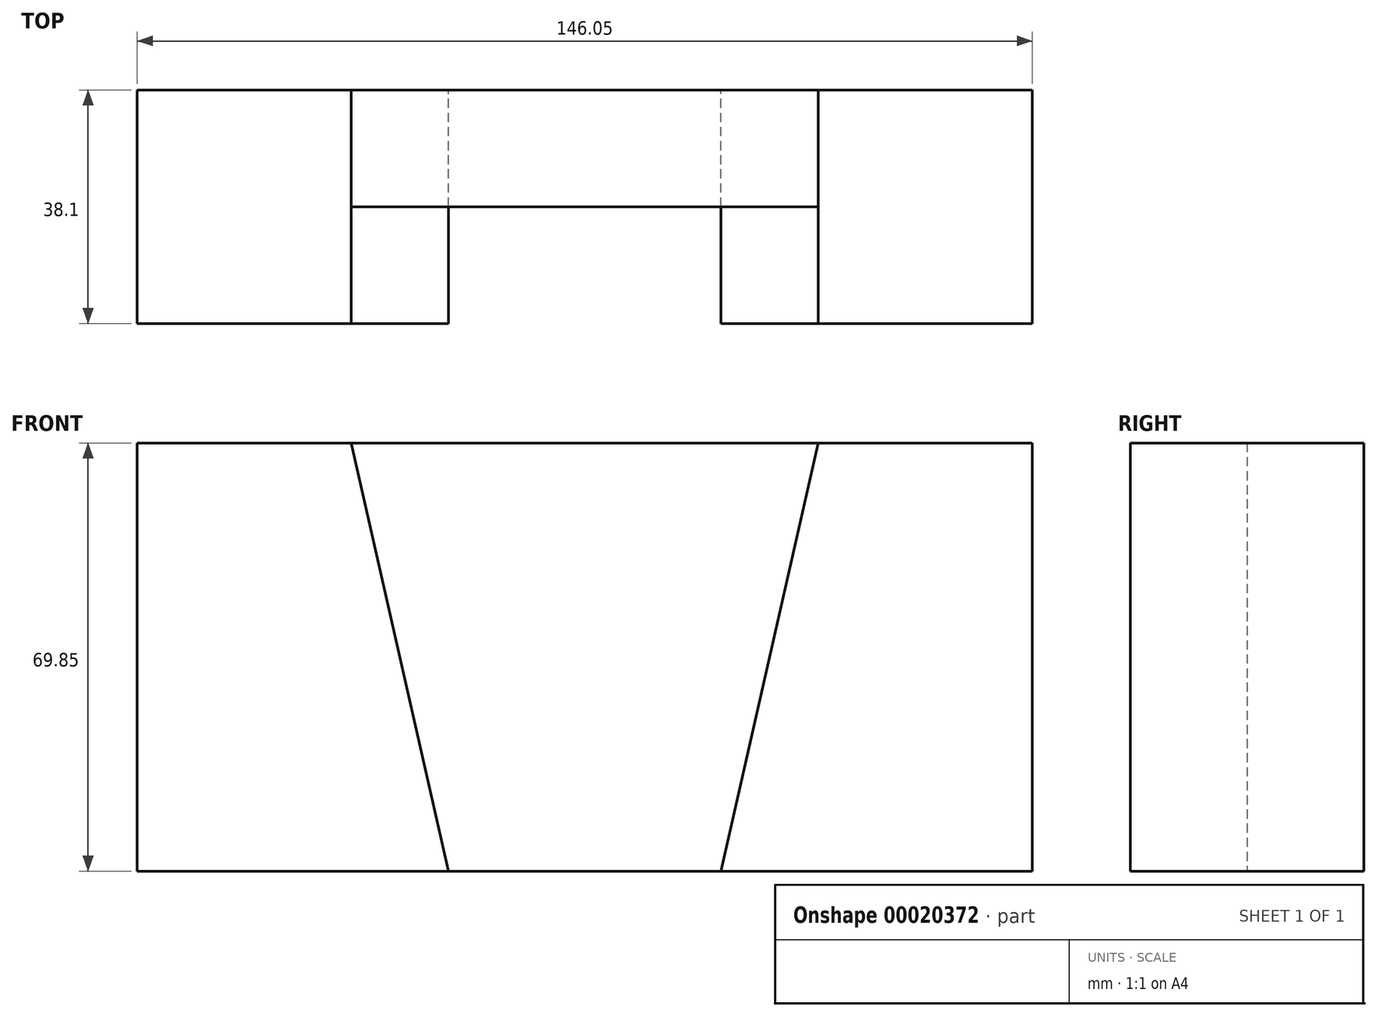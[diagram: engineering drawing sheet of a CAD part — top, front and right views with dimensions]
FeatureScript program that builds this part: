
annotation { "Feature Type Name" : "Feature", "Feature Type Description" : "" }
export const myFeature = defineFeature(function(context is Context, id is Id, definition is map)
    precondition{}
    {
        {
            var Q0;
            Q0=qCreatedBy(makeId("Front.planeOp"),FACE);
            var sketch = newSketch(context, id + "F0", { "sketchPlane" : qUnion([Q0])});
            skLineSegment(sketch, "E0.bottom", {"start": v(-82.58, 22.66) * mm, "end": v(63.47, 22.66) * mm});
            skLineSegment(sketch, "E0.top", {"start": v(-82.58, -47.19) * mm, "end": v(63.47, -47.19) * mm});
            skLineSegment(sketch, "E0.left", {"start": v(-82.58, 22.66) * mm, "end": v(-82.58, -47.19) * mm});
            skLineSegment(sketch, "E0.right", {"start": v(63.47, 22.66) * mm, "end": v(63.47, -47.19) * mm});
            skPoint(sketch, "E1", {"position": v(-31.78, -47.19) * mm});
            skPoint(sketch, "E2", {"position": v(12.67, -47.19) * mm});
            skPoint(sketch, "E3", {"position": v(-47.66, 22.66) * mm});
            skPoint(sketch, "E4", {"position": v(28.54, 22.66) * mm});
            skLineSegment(sketch, "E5", {"start": v(-47.66, 22.66) * mm, "end": v(-31.78, -47.19) * mm});
            skLineSegment(sketch, "E6", {"start": v(28.54, 22.66) * mm, "end": v(12.67, -47.19) * mm});
            skSolve(sketch);
        }
        {
            var Q0;
            {var subQ1=sQuery(id+"F0.wireOp",EDGE,"E0.right");Q0=makeQuery(id+"F0.imprint","IMPRINT",FACE,{"disambiguationData":[TD([[makeQuery(id+"F0.imprint","IMPRINT",EDGE,{"derivedFrom":subQ1}),-1.0]])]});}
            var Q1;
            {var subQ1=sQuery(id+"F0.wireOp",EDGE,"E0.left");Q1=makeQuery(id+"F0.imprint","IMPRINT",FACE,{"disambiguationData":[TD([[makeQuery(id+"F0.imprint","IMPRINT",EDGE,{"derivedFrom":subQ1}),1.0]])]});}
            extrude(context, id + "F1", {"entities" : qUnion([Q0, Q1]), "depth" : 38.1 * mm});
        }
        {
            var Q0;
            {var subQ1=sQuery(id+"F0.wireOp",EDGE,"E5");Q0=makeQuery(id+"F0.imprint","IMPRINT",FACE,{"disambiguationData":[TD([[makeQuery(id+"F0.imprint","IMPRINT",EDGE,{"derivedFrom":subQ1}),1.0]])]});}
            extrude(context, id + "F2", {"entities" : qUnion([Q0]), "depth" : 19.05 * mm});
        }
    });
